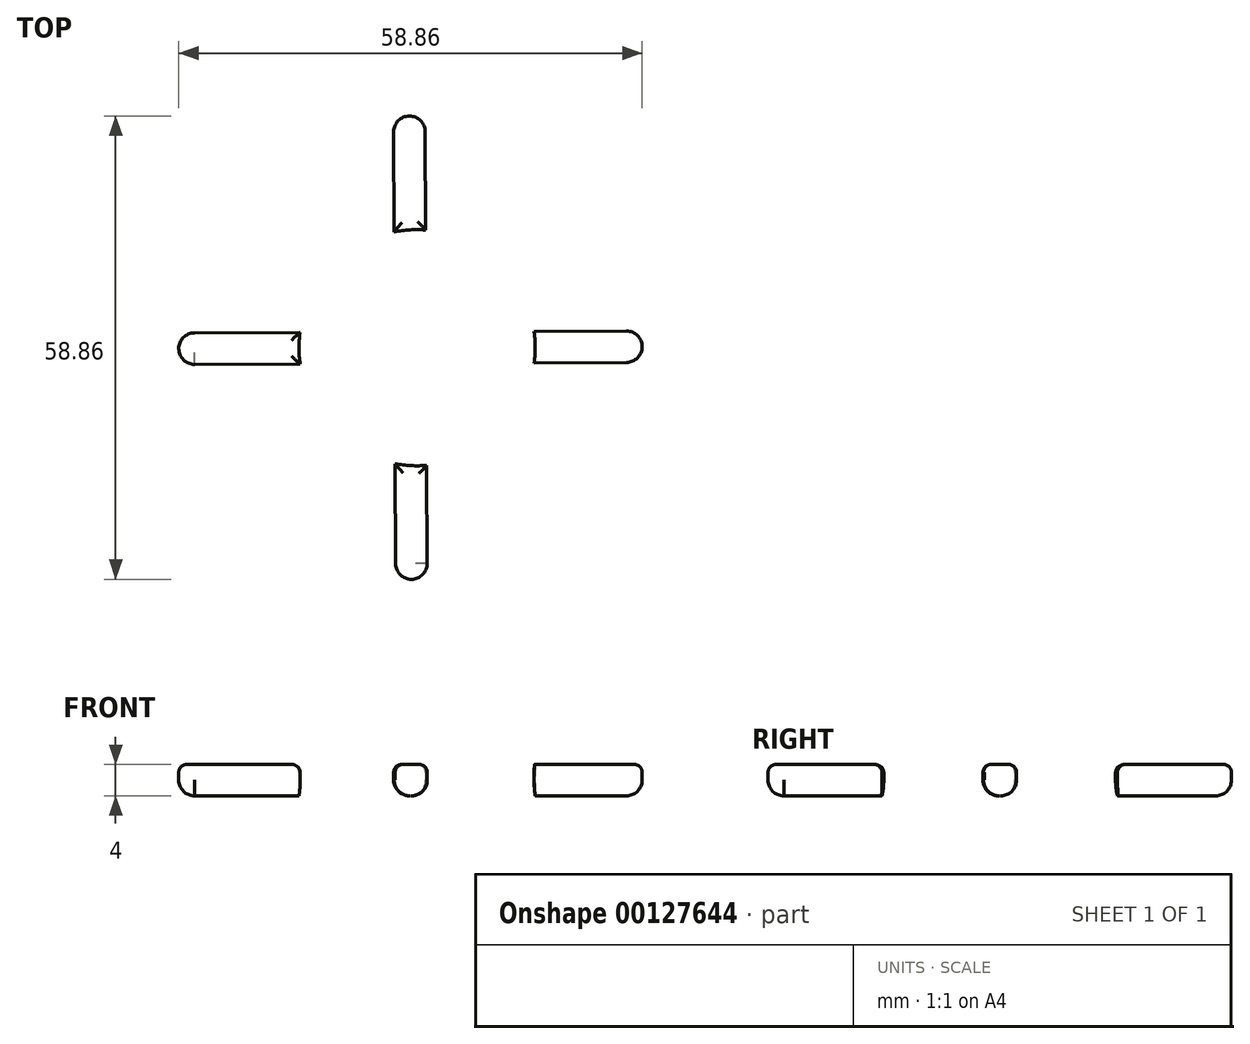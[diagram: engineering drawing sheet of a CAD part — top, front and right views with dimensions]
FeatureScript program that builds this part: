
annotation { "Feature Type Name" : "Feature", "Feature Type Description" : "" }
export const myFeature = defineFeature(function(context is Context, id is Id, definition is map)
    precondition{}
    {
        {
            var Q0;
            Q0=qCreatedBy(makeId("Top.planeOp"),FACE);
            var sketch = newSketch(context, id + "F0", { "sketchPlane" : qUnion([Q0])});
            skCircle(sketch, "E0.cCircle", {"center": v(0, 0) * mm, "radius": 27.5 * mm, "construction": true});
            skPoint(sketch, "E0.0.midPoint", {"position": v(19.36, 19.53) * mm});
            skLineSegment(sketch, "E1.trimOffspring", {"start": v(1.93, 14.96) * mm, "end": v(1.88, 27.44) * mm});
            skLineSegment(sketch, "E2.trimOffspring", {"start": v(15.72, -1.93) * mm, "end": v(27.44, -1.88) * mm});
            skLineSegment(sketch, "E3.trimOffspring", {"start": v(-2.07, 14.71) * mm, "end": v(-2.12, 27.42) * mm});
            skLineSegment(sketch, "E4.trimOffspring", {"start": v(15.7, 2.07) * mm, "end": v(27.42, 2.12) * mm});
            skLineSegment(sketch, "E5.trimOffspring", {"start": v(-27.44, 1.88) * mm, "end": v(-14.03, 1.94) * mm});
            skLineSegment(sketch, "E6.trimOffspring", {"start": v(-27.42, -2.12) * mm, "end": v(-14.01, -2.06) * mm});
            skPoint(sketch, "E7.orphan", {"position": v(-38.9, -0.17) * mm});
            skLineSegment(sketch, "E8.trimOffspring", {"start": v(2.12, -27.42) * mm, "end": v(2.07, -14.95) * mm});
            skLineSegment(sketch, "E9.trimOffspring", {"start": v(-1.88, -27.44) * mm, "end": v(-1.93, -14.74) * mm});
            skPoint(sketch, "E10.orphan", {"position": v(38.9, 0.17) * mm});
            skArc(sketch, "E11", {"start": v(-1.88, -27.44) * mm, "mid": v(0.13, -29.43) * mm, "end": v(2.12, -27.42) * mm});
            skArc(sketch, "E12", {"start": v(27.44, -1.88) * mm, "mid": v(29.43, 0.13) * mm, "end": v(27.42, 2.12) * mm});
            skArc(sketch, "E13", {"start": v(-2.12, 27.42) * mm, "mid": v(-0.13, 29.43) * mm, "end": v(1.88, 27.44) * mm});
            skArc(sketch, "E14", {"start": v(-27.42, -2.12) * mm, "mid": v(-29.43, -0.13) * mm, "end": v(-27.44, 1.88) * mm});
            skArc(sketch, "E15", {"start": v(-1.93, -14.74) * mm, "mid": v(0.06, -14.98) * mm, "end": v(2.07, -14.95) * mm});
            skArc(sketch, "E16.trimOffspring", {"start": v(-14.03, 1.94) * mm, "mid": v(-14.15, -0.06) * mm, "end": v(-14.01, -2.06) * mm});
            skArc(sketch, "E17.trimOffspring", {"start": v(15.72, -1.93) * mm, "mid": v(15.85, 0.07) * mm, "end": v(15.7, 2.07) * mm});
            skArc(sketch, "E18.trimOffspring", {"start": v(1.93, 14.96) * mm, "mid": v(-0.07, 14.97) * mm, "end": v(-2.07, 14.71) * mm});
            skSolve(sketch);
        }
        {
            var Q0;
            Q0 = qSketchRegion(id + "F0", true);
            extrude(context, id + "F1", {"entities" : qUnion([Q0]), "depth" : 4 * mm});
        }
        {
            var Q0;
            Q0=makeQuery(id+"F1.opExtrude","CAP_EDGE",EDGE,{"disambiguationData":[OSD([sQuery(id+"F0.wireOp",EDGE,"E8.trimOffspring")])],"isStart":true});
            var Q1;
            Q1=makeQuery(id+"F1.opExtrude","CAP_EDGE",EDGE,{"disambiguationData":[OSD([sQuery(id+"F0.wireOp",EDGE,"E2.trimOffspring")])],"isStart":true});
            var Q2;
            Q2=makeQuery(id+"F1.opExtrude","CAP_EDGE",EDGE,{"disambiguationData":[OSD([sQuery(id+"F0.wireOp",EDGE,"E1.trimOffspring")])],"isStart":true});
            var Q3;
            Q3=makeQuery(id+"F1.opExtrude","CAP_EDGE",EDGE,{"disambiguationData":[OSD([sQuery(id+"F0.wireOp",EDGE,"E6.trimOffspring")])],"isStart":true});
            fillet(context, id + "F2", {"entities" : qUnion([Q0, Q1, Q2, Q3]), "radius" : 2 * mm, "tangentPropagation" : true, "allowEdgeOverflow" : false});
        }
        {
            var Q0;
            Q0=makeQuery(id+"F1.opExtrude","CAP_FACE",FACE,{"disambiguationData":[OSD([sQuery(id+"F0.wireOp",EDGE,"E8.trimOffspring"),sQuery(id+"F0.wireOp",EDGE,"E9.trimOffspring"),sQuery(id+"F0.wireOp",EDGE,"E11"),sQuery(id+"F0.wireOp",EDGE,"E15")])],"isStart":false});
            var Q1;
            Q1=makeQuery(id+"F1.opExtrude","CAP_EDGE",EDGE,{"disambiguationData":[OSD([sQuery(id+"F0.wireOp",EDGE,"E2.trimOffspring")])],"isStart":false});
            var Q2;
            Q2=makeQuery(id+"F1.opExtrude","CAP_FACE",FACE,{"disambiguationData":[OSD([sQuery(id+"F0.wireOp",EDGE,"E1.trimOffspring"),sQuery(id+"F0.wireOp",EDGE,"E3.trimOffspring"),sQuery(id+"F0.wireOp",EDGE,"E13"),sQuery(id+"F0.wireOp",EDGE,"E18.trimOffspring")])],"isStart":false});
            var Q3;
            Q3=makeQuery(id+"F1.opExtrude","CAP_FACE",FACE,{"disambiguationData":[OSD([sQuery(id+"F0.wireOp",EDGE,"E5.trimOffspring"),sQuery(id+"F0.wireOp",EDGE,"E6.trimOffspring"),sQuery(id+"F0.wireOp",EDGE,"E14"),sQuery(id+"F0.wireOp",EDGE,"E16.trimOffspring")])],"isStart":false});
            fillet(context, id + "F3", {"entities" : qUnion([Q0, Q1, Q2, Q3]), "radius" : 1 * mm, "tangentPropagation" : true, "allowEdgeOverflow" : false});
        }
    });
